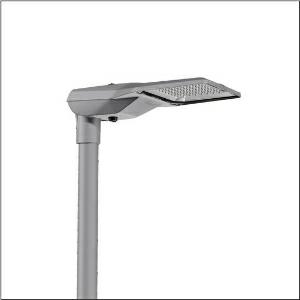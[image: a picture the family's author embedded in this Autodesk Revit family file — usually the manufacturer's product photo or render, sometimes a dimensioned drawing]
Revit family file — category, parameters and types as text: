
# Revit family: streetlight_sl_21_midi___st1_0ab_5xe3m33t08lb_f14d
name_source: partatom
category: Lighting Fixtures
units: mm (PartAtom-declared; Revit-internal decimal feet)

## family parameters
Cut with Voids When Loaded = No
Host = Face
Light Source = No
Part Type = Normal
Room Calculation Point = No
Round Connector Dimension = Use Diameter
Shared = No

## types (1)
- --- (1 x LED, 12620 lm, 99.6 W, 3000K)
    Apparent Load = 100 VA
    CIE Flux Codes = 38 73 97 100 100
    Color Rendering = 70
    Color Temperature = 3000K
    Default Elevation = 1800 mm
    Description = Streetlight SL 21 midi, mast luminaire, primary light control with lens, of PMMA, primary optical cover: cover, of toughened safety glass, transparent, light distribution: ST1.0aB, light emission: direct distribution, primary light characteristic: asymmetric, installation type: side-entry, post-top, LED, High Power LED, rated luminous flux: 12.620lm, luminous efficacy: 127lm/W, light colour: 730, colour temperature: 3000K, control gear: D4i, control: flexible luminous flux parameterisation, time-dependent luminous flux control, constant luminous flux control, overheat protection, pre-setting: logarithmic dimming characteristic, mains connection: 230..240V, AC, 50/60Hz, start of lifetime: 100W, end of service life: 102W, reduction: 46W, luminaire housing, of diecast aluminium, powder-coated, Siteco® metallic grey (DB 702S), corrosivity category C5 mid according to DIN EN ISO 12944, please order mast flange separately, inclination adjustable: 0°, 5°, 10°, 15°, sealing non-destructively replaceable, multi-level sealing system, length: 644mm, width: 335mm, height: 110mm, mast flange for spigot size: 42mm (side-entry): 5XC10008XM4, 60/48mm (side-entry/post-top): 5XC10108XM2, 76/60mm (side-entry/post-top): 5XC10108XM1, mounting height: 4..8m, Smart Interface below and above, protection rating (complete): IP66, insulation class (complete): insulation class II (safety insulation), certification: CE, ENEC, ENEC+, VDE, impact resistance: IK10, permissible operating ambient temperature for outdoor applications: -40..+50°C, standard-compliant lighting for roads and squares, packaging unit: 1 piece

Light Distribution: ST1.0aB
    Height = 111 mm
    Lamp = 1 x LED
    Lamp Light Flux = 12620 lm
    Lamp Power = 99.6 W
    Lamp count = 1
    Length = 644 mm
    Luminous efficacy = 127 lm/W
    Manufacturer = Siteco
    ModVariant = No
    Model = 5XE3M33T08LB
    Number of Poles = 1
    OnlyDefault = Yes
    Power Factor = 1
    Product Name = Streetlight SL 21 midi | ST1.0aB
    Product group = mast luminaire | pylon top
    ProductGroupID = 6100
    Protection Class = Protection class II
    Protection Degree = IP 66
    RLX_Detail_Level = 1
    RLX_Emergency_Light_Flux = 0 lm
    RLX_Emergency_Type = 0
    RLX_Emergency_Type_DB = No
    RlxData = <blob elided: 26949 chars, md5=47cef0bd>
    Socket = socket
    Standby Power = 0 W
    System Light Flux = 12620 lm
    System Power = 100 W
    Type Comments = factory setting: luminous flux: 100 % | dim-lin: 254 | 1020 mA
    Type Image = l_1004304.jpg
    URL = http://relux.com
    VarID = @adj_010997
    Voltage = 0 V
    Weight = 0.00 kg
    Width = 336 mm

## geometry (parser evidence)
native form markers: Blend x4, Sweep x11
no freeform markers — native parametric forms only
